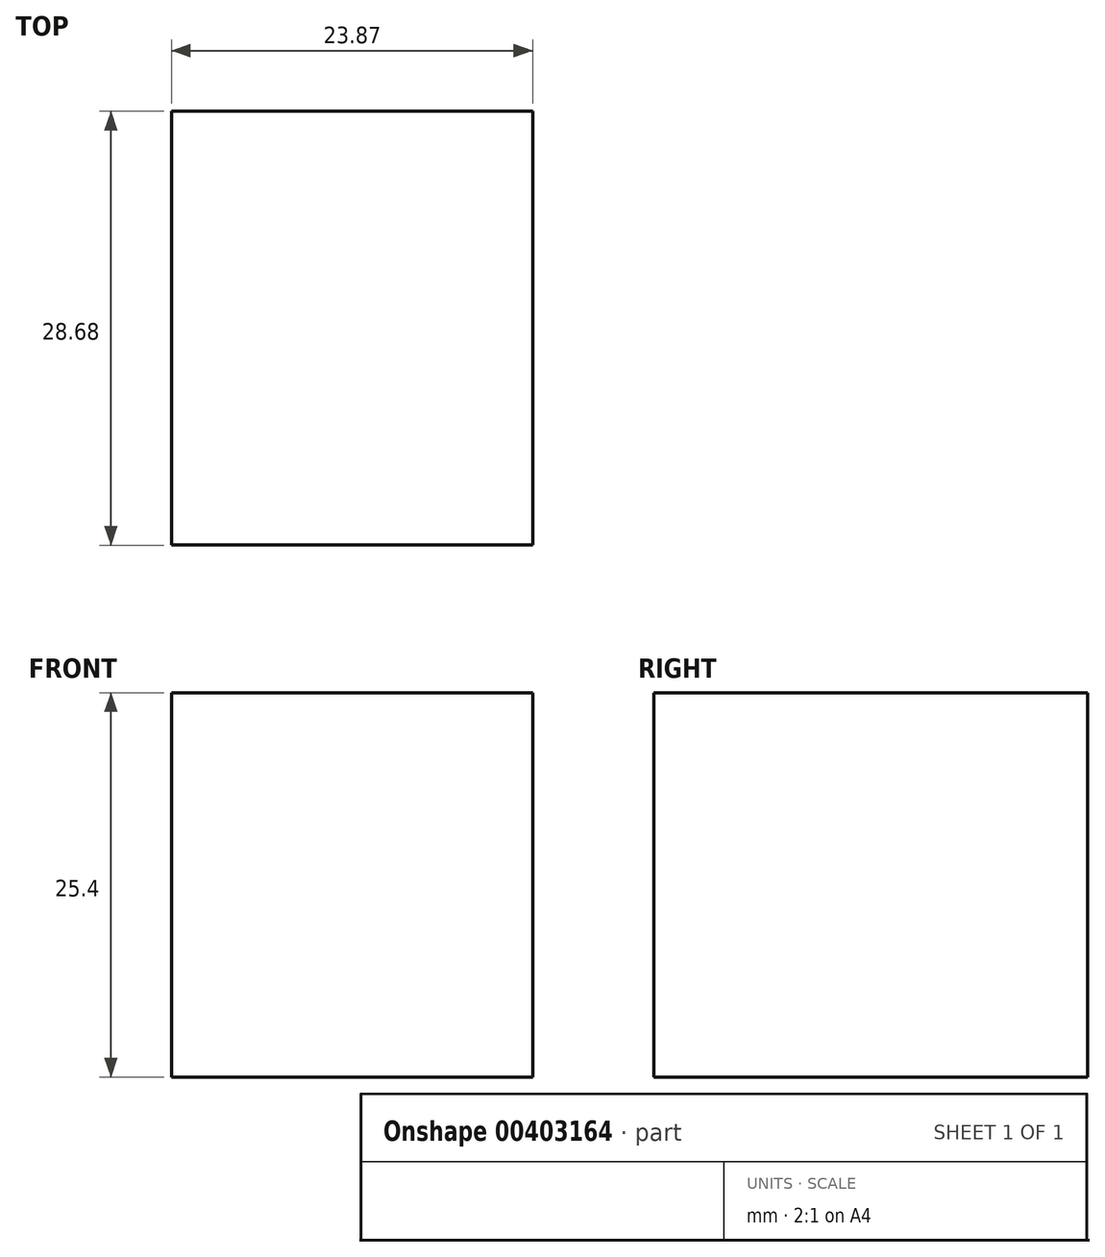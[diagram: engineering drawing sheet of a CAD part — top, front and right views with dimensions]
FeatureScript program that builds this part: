
annotation { "Feature Type Name" : "Feature", "Feature Type Description" : "" }
export const myFeature = defineFeature(function(context is Context, id is Id, definition is map)
    precondition{}
    {
        {
            var Q0;
            Q0=qCreatedBy(makeId("Top.planeOp"),FACE);
            var sketch = newSketch(context, id + "F0", { "sketchPlane" : qUnion([Q0])});
            skLineSegment(sketch, "E0.bottom", {"start": v(-3.08, 6.16) * mm, "end": v(20.8, 6.16) * mm});
            skLineSegment(sketch, "E0.top", {"start": v(-3.08, -22.52) * mm, "end": v(20.8, -22.52) * mm});
            skLineSegment(sketch, "E0.left", {"start": v(-3.08, 6.16) * mm, "end": v(-3.08, -22.52) * mm});
            skLineSegment(sketch, "E0.right", {"start": v(20.8, 6.16) * mm, "end": v(20.8, -22.52) * mm});
            skSolve(sketch);
        }
        {
            var Q0;
            Q0 = qSketchRegion(id + "F0", true);
            extrude(context, id + "F1", {"entities" : qUnion([Q0]), "depth" : 25.4 * mm});
        }
    });
